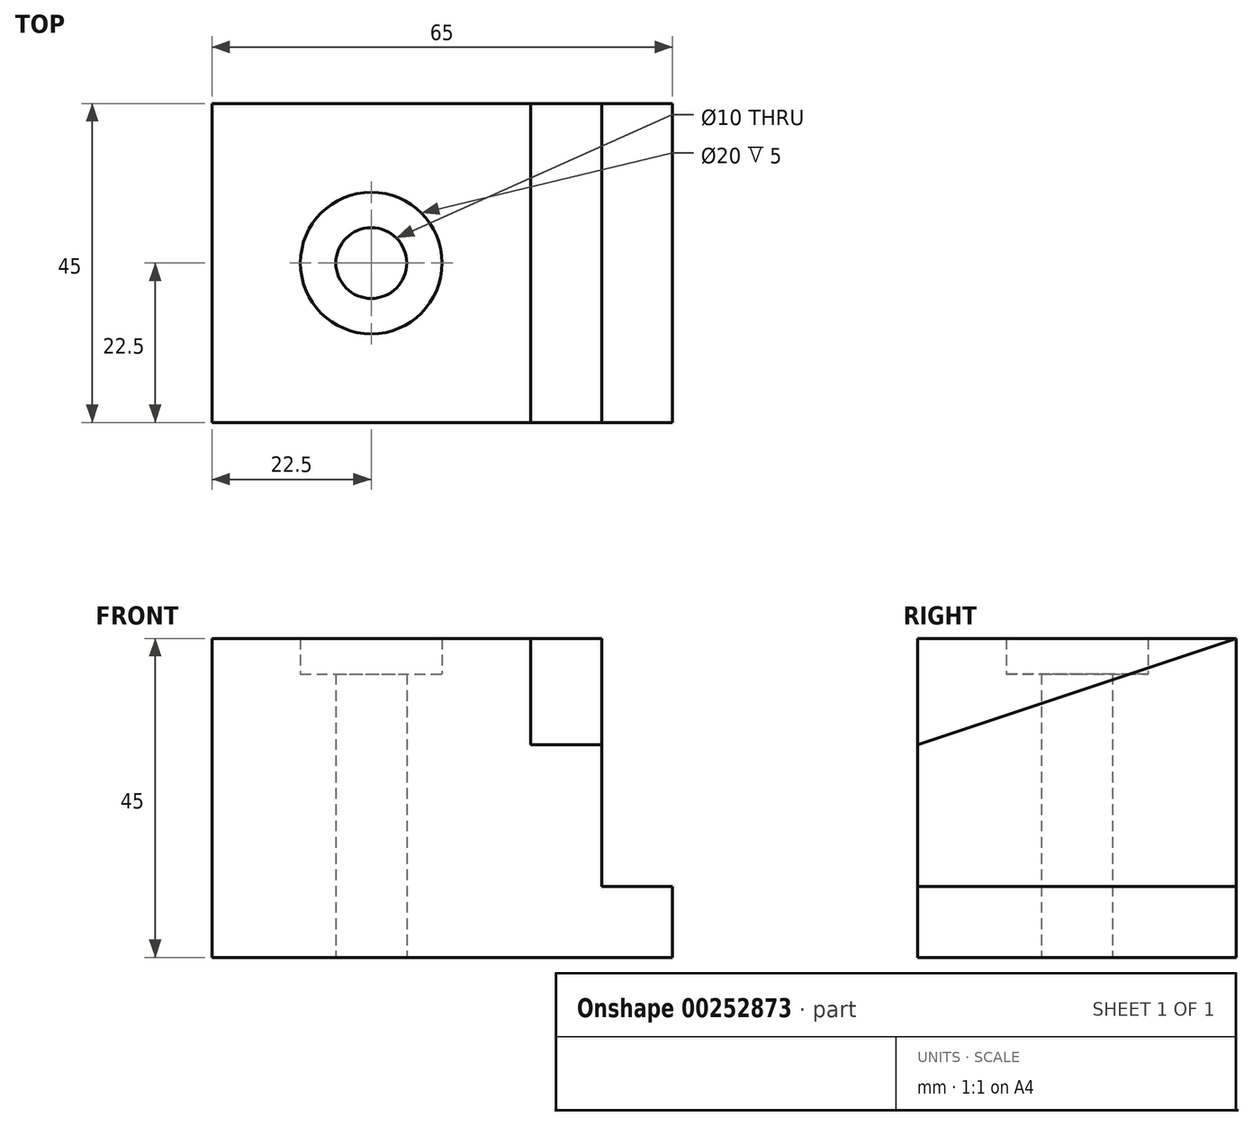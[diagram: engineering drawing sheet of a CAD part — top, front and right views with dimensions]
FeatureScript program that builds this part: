
annotation { "Feature Type Name" : "Feature", "Feature Type Description" : "" }
export const myFeature = defineFeature(function(context is Context, id is Id, definition is map)
    precondition{}
    {
        {
            var Q0;
            Q0=qCreatedBy(makeId("Front.planeOp"),FACE);
            var sketch = newSketch(context, id + "F0", { "sketchPlane" : qUnion([Q0])});
            skLineSegment(sketch, "E0.bottom", {"start": v(0, 0) * mm, "end": v(65, 0) * mm});
            skLineSegment(sketch, "E0.top", {"start": v(0, 45) * mm, "end": v(55, 45) * mm});
            skLineSegment(sketch, "E0.left", {"start": v(0, 0) * mm, "end": v(0, 45) * mm});
            skLineSegment(sketch, "E0.right", {"start": v(65, 0) * mm, "end": v(65, 10) * mm});
            skLineSegment(sketch, "E1", {"start": v(65, 10) * mm, "end": v(55, 10) * mm});
            skLineSegment(sketch, "E2", {"start": v(55, 10) * mm, "end": v(55, 45) * mm});
            skSolve(sketch);
        }
        {
            var Q0;
            Q0=makeQuery(id+"F0.imprint","IMPRINT",FACE,{"disambiguationData":[TD([[makeQuery(id+"F0.imprint","IMPRINT",EDGE,{"derivedFrom":sQuery(id+"F0.wireOp",EDGE,"E0.bottom")}),1.0]])]});
            extrude(context, id + "F1", {"entities" : qUnion([Q0]), "depth" : 45 * mm, "symmetric" : true});
        }
        {
            var Q0;
            Q0=makeQuery(id+"F1.opExtrude","SWEPT_FACE",FACE,{"disambiguationData":[OSD([sQuery(id+"F0.wireOp",EDGE,"E2")])]});
            var sketch = newSketch(context, id + "F2", { "sketchPlane" : qUnion([Q0])});
            skLineSegment(sketch, "E3", {"start": v(-22.5, 30) * mm, "end": v(22.5, 45) * mm});
            skSolve(sketch);
        }
        {
            var Q0;
            {var subQ0=sQuery(id+"F2.wireOp",EDGE,"E3");Q0=makeQuery(id+"F2.imprint","IMPRINT",FACE,{"disambiguationData":[TD([[makeQuery(id+"F2.imprint","IMPRINT",EDGE,{"derivedFrom":subQ0}),1.0]])]});}
            extrude(context, id + "F3", {"entities" : qUnion([Q0]), "operationType" : NewBodyOperationType.REMOVE, "oppositeDirection" : true, "depth" : 10 * mm});
        }
        {
            var Q0;
            Q0=makeQuery(id+"F1.opExtrude","SWEPT_FACE",FACE,{"disambiguationData":[OSD([sQuery(id+"F0.wireOp",EDGE,"E0.top")])]});
            var sketch = newSketch(context, id + "F4", { "sketchPlane" : qUnion([Q0])});
            skPoint(sketch, "E4", {"position": v(22.5, 0) * mm});
            skSolve(sketch);
        }
        {
            var Q0;
            Q0=sQuery(id+"F4.wireOp",VERTEX,"E4");
            var Q1;
            Q1=makeQuery(id+"F1.opExtrude","SWEPT_BODY",BODY,{"disambiguationData":[OSD([sQuery(id+"F0.wireOp",EDGE,"E0.bottom"),sQuery(id+"F0.wireOp",EDGE,"E0.top"),sQuery(id+"F0.wireOp",EDGE,"E0.left"),sQuery(id+"F0.wireOp",EDGE,"E0.right"),sQuery(id+"F0.wireOp",EDGE,"E1"),sQuery(id+"F0.wireOp",EDGE,"E2")])]});
            hole(context, id + "F5", {"style" : HoleStyle.C_BORE, "endStyle" : HoleEndStyle.THROUGH, "holeDiameter" : 10 * mm, "cBoreDiameter" : 20 * mm, "cBoreDepth" : 5 * mm, "tappedDepth" : 12 * mm, "tapClearance" : 3, "locations" : qUnion([Q0]), "scope" : qUnion([Q1])});
        }
    });
